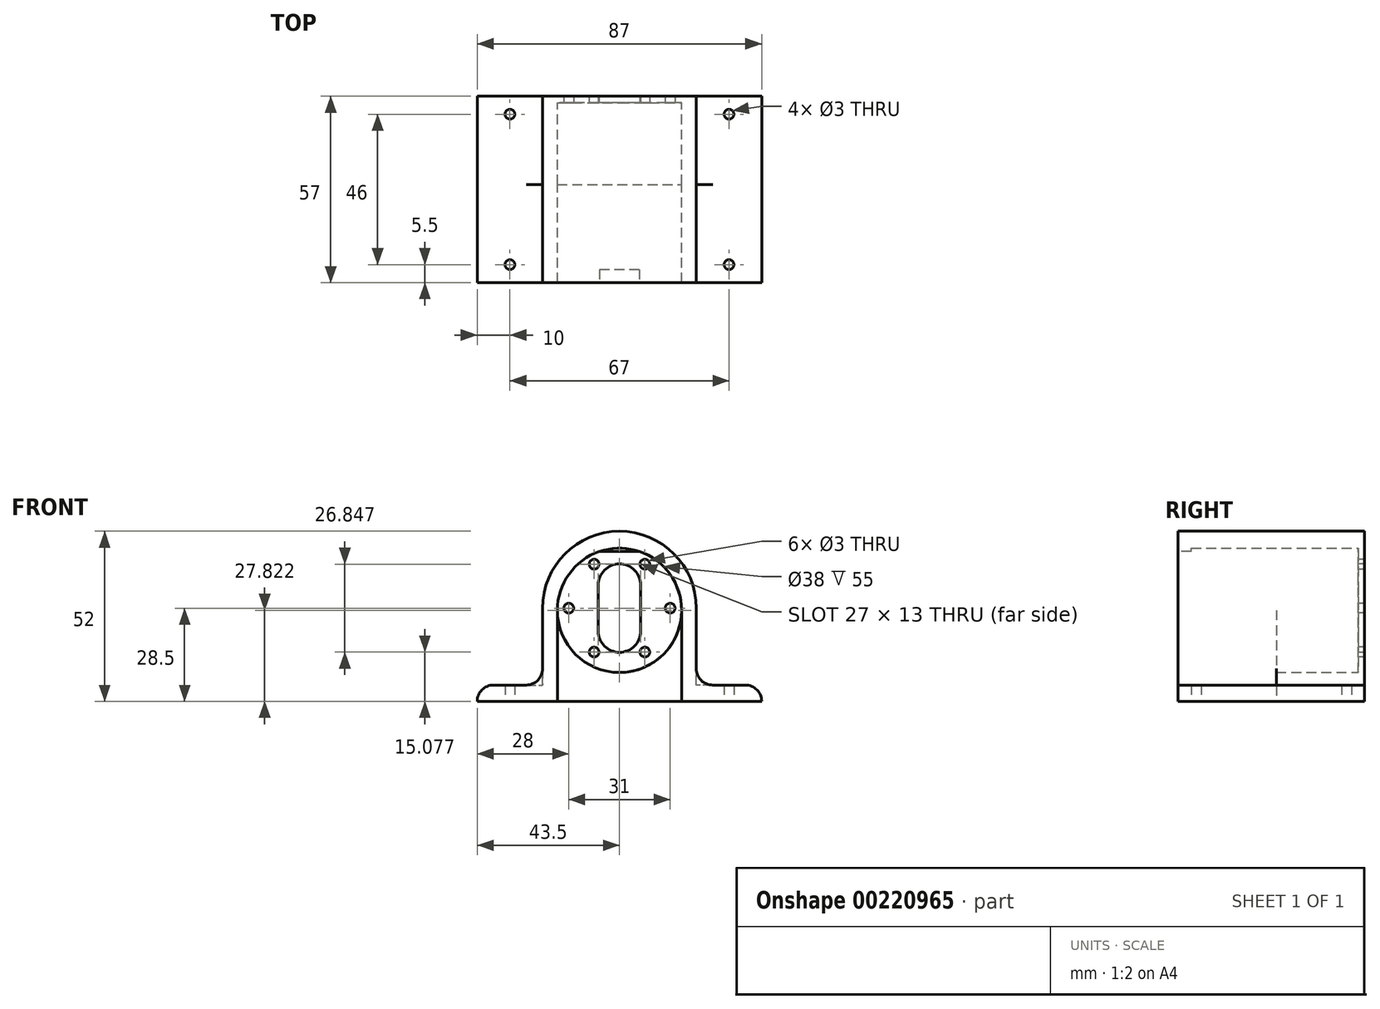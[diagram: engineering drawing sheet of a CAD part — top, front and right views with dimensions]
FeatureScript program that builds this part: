
annotation { "Feature Type Name" : "Feature", "Feature Type Description" : "" }
export const myFeature = defineFeature(function(context is Context, id is Id, definition is map)
    precondition{}
    {
        {
            var Q0;
            Q0=qCreatedBy(makeId("Front.planeOp"),FACE);
            var sketch = newSketch(context, id + "F0", { "sketchPlane" : qUnion([Q0])});
            skLineSegment(sketch, "E0", {"start": v(0, -23.5) * mm, "end": v(-23.5, -23.5) * mm});
            skLineSegment(sketch, "E1", {"start": v(-23.5, -23.5) * mm, "end": v(-23.5, 0) * mm});
            skLineSegment(sketch, "E2", {"start": v(0, -23.5) * mm, "end": v(23.5, -23.5) * mm});
            skLineSegment(sketch, "E3", {"start": v(23.5, -23.5) * mm, "end": v(23.5, 0) * mm});
            skArc(sketch, "E4", {"start": v(-23.5, 0) * mm, "mid": v(0, 23.5) * mm, "end": v(23.5, 0) * mm});
            skSolve(sketch);
        }
        {
            var Q0;
            Q0=qSketchRegion(id+"F0",true);
            extrude(context, id + "F1", {"entities" : qUnion([Q0]), "depth" : 2 * mm});
        }
        {
            var Q0;
            Q0=makeQuery(id+"F1.opExtrude","CAP_FACE",FACE,{"disambiguationData":[OSD([sQuery(id+"F0.wireOp",EDGE,"E0"),sQuery(id+"F0.wireOp",EDGE,"E1"),sQuery(id+"F0.wireOp",EDGE,"E2"),sQuery(id+"F0.wireOp",EDGE,"E3"),sQuery(id+"F0.wireOp",EDGE,"E4")])],"isStart":false});
            var sketch = newSketch(context, id + "F2", { "sketchPlane" : qUnion([Q0])});
            skCircle(sketch, "E5", {"center": v(15.5, 0) * mm, "radius": 1.5 * mm});
            skCircle(sketch, "E6.1.0", {"center": v(7.75, 13.42) * mm, "radius": 1.5 * mm});
            skCircle(sketch, "E6.2.0", {"center": v(-7.75, 13.42) * mm, "radius": 1.5 * mm});
            skCircle(sketch, "E6.3.0", {"center": v(-15.5, 0) * mm, "radius": 1.5 * mm});
            skCircle(sketch, "E6.4.0", {"center": v(-7.75, -13.42) * mm, "radius": 1.5 * mm});
            skCircle(sketch, "E6.5.0", {"center": v(7.75, -13.42) * mm, "radius": 1.5 * mm});
            skPoint(sketch, "E6.center", {"position": v(0, 0) * mm});
            skLineSegment(sketch, "E7", {"start": v(6.5, 7) * mm, "end": v(6.5, -7) * mm});
            skLineSegment(sketch, "E8", {"start": v(-6.5, -7) * mm, "end": v(-6.5, 7) * mm});
            skArc(sketch, "E9", {"start": v(-6.5, 7) * mm, "mid": v(0, 13.5) * mm, "end": v(6.5, 7) * mm});
            skArc(sketch, "E10", {"start": v(-6.5, -7) * mm, "mid": v(0, -13.5) * mm, "end": v(6.5, -7) * mm});
            skSolve(sketch);
        }
        {
            var Q0;
            Q0=qSketchRegion(id+"F2",true);
            extrude(context, id + "F3", {"entities" : qUnion([Q0]), "operationType" : NewBodyOperationType.REMOVE, "oppositeDirection" : true, "depth" : 5 * mm});
        }
        {
            var Q0;
            Q0=qCreatedBy(makeId("Front.planeOp"),FACE);
            var sketch = newSketch(context, id + "F4", { "sketchPlane" : qUnion([Q0])});
            skCircle(sketch, "E11", {"center": v(0, -0.68) * mm, "radius": 19 * mm});
            skLineSegment(sketch, "E12", {"start": v(-23.5, 0) * mm, "end": v(-23.5, -23.5) * mm});
            skLineSegment(sketch, "E13", {"start": v(-23.5, -23.5) * mm, "end": v(23.5, -23.5) * mm});
            skLineSegment(sketch, "E14", {"start": v(23.5, -23.5) * mm, "end": v(23.5, 0) * mm});
            skArc(sketch, "E15", {"start": v(-23.5, 0) * mm, "mid": v(0, 23.5) * mm, "end": v(23.5, 0) * mm});
            skSolve(sketch);
        }
        {
            var Q0;
            Q0=qSketchRegion(id+"F4",true);
            extrude(context, id + "F5", {"entities" : qUnion([Q0]), "operationType" : NewBodyOperationType.ADD, "offsetDistance" : 25 * mm, "depth" : 27 * mm});
        }
        {
            var Q0;
            Q0=makeQuery(id+"F5.boolean.opBoolean","MERGE",FACE,{"derivedFrom":[makeQuery(id+"F1.opExtrude","SWEPT_FACE",FACE,{"disambiguationData":[OSD([sQuery(id+"F0.wireOp",EDGE,"E0"),sQuery(id+"F0.wireOp",EDGE,"E2")])]}),makeQuery(id+"F5.opExtrude","SWEPT_FACE",FACE,{"disambiguationData":[OSD([sQuery(id+"F4.wireOp",EDGE,"E13")])]})]});
            var sketch = newSketch(context, id + "F6", { "sketchPlane" : qUnion([Q0])});
            skLineSegment(sketch, "E16.bottom", {"start": v(-23.5, 27) * mm, "end": v(23.5, 27) * mm});
            skLineSegment(sketch, "E16.top", {"start": v(-23.5, 0) * mm, "end": v(23.5, 0) * mm});
            skLineSegment(sketch, "E16.left", {"start": v(-23.5, 27) * mm, "end": v(-23.5, 0) * mm});
            skLineSegment(sketch, "E16.right", {"start": v(23.5, 27) * mm, "end": v(23.5, 0) * mm});
            skSolve(sketch);
        }
        {
            var Q0;
            Q0=qSketchRegion(id+"F6",true);
            extrude(context, id + "F7", {"entities" : qUnion([Q0]), "operationType" : NewBodyOperationType.ADD, "depth" : 5 * mm});
        }
        {
            var Q0;
            Q0=makeQuery(id+"F7.boolean.opBoolean","MERGE",FACE,{"derivedFrom":[makeQuery(id+"F5.boolean.opBoolean","MERGE",FACE,{"derivedFrom":[makeQuery(id+"F1.opExtrude","SWEPT_FACE",FACE,{"disambiguationData":[OSD([sQuery(id+"F0.wireOp",EDGE,"E1")])]}),makeQuery(id+"F5.opExtrude","SWEPT_FACE",FACE,{"disambiguationData":[OSD([sQuery(id+"F4.wireOp",EDGE,"E12")])]})]}),makeQuery(id+"F7.opExtrude","SWEPT_FACE",FACE,{"disambiguationData":[OSD([sQuery(id+"F6.wireOp",EDGE,"E16.left")])]})]});
            var sketch = newSketch(context, id + "F8", { "sketchPlane" : qUnion([Q0])});
            skLineSegment(sketch, "E17.bottom", {"start": v(0, -28.5) * mm, "end": v(27, -28.5) * mm});
            skLineSegment(sketch, "E17.top", {"start": v(0, -23.5) * mm, "end": v(27, -23.5) * mm});
            skLineSegment(sketch, "E17.left", {"start": v(0, -28.5) * mm, "end": v(0, -23.5) * mm});
            skLineSegment(sketch, "E17.right", {"start": v(27, -28.5) * mm, "end": v(27, -23.5) * mm});
            skSolve(sketch);
        }
        {
            var Q0;
            Q0=qSketchRegion(id+"F8",true);
            extrude(context, id + "F9", {"entities" : qUnion([Q0]), "operationType" : NewBodyOperationType.ADD, "depth" : 20 * mm});
        }
        {
            var Q0;
            Q0=makeQuery(id+"F7.boolean.opBoolean","MERGE",FACE,{"derivedFrom":[makeQuery(id+"F5.boolean.opBoolean","MERGE",FACE,{"derivedFrom":[makeQuery(id+"F1.opExtrude","SWEPT_FACE",FACE,{"disambiguationData":[OSD([sQuery(id+"F0.wireOp",EDGE,"E3")])]}),makeQuery(id+"F5.opExtrude","SWEPT_FACE",FACE,{"disambiguationData":[OSD([sQuery(id+"F4.wireOp",EDGE,"E14")])]})]}),makeQuery(id+"F7.opExtrude","SWEPT_FACE",FACE,{"disambiguationData":[OSD([sQuery(id+"F6.wireOp",EDGE,"E16.right")])]})]});
            var sketch = newSketch(context, id + "F10", { "sketchPlane" : qUnion([Q0])});
            skLineSegment(sketch, "E18.bottom", {"start": v(-27, -28.5) * mm, "end": v(0, -28.5) * mm});
            skLineSegment(sketch, "E18.top", {"start": v(-27, -23.5) * mm, "end": v(0, -23.5) * mm});
            skLineSegment(sketch, "E18.left", {"start": v(-27, -28.5) * mm, "end": v(-27, -23.5) * mm});
            skLineSegment(sketch, "E18.right", {"start": v(0, -28.5) * mm, "end": v(0, -23.5) * mm});
            skSolve(sketch);
        }
        {
            var Q0;
            Q0=qSketchRegion(id+"F10",true);
            extrude(context, id + "F11", {"entities" : qUnion([Q0]), "operationType" : NewBodyOperationType.ADD, "depth" : 20 * mm});
        }
        {
            var Q0;
            Q0=makeQuery(id+"F11.opExtrude","CAP_EDGE",EDGE,{"disambiguationData":[OSD([sQuery(id+"F10.wireOp",EDGE,"E18.top")])],"isStart":true});
            var Q1;
            Q1=makeQuery(id+"F11.opExtrude","CAP_EDGE",EDGE,{"disambiguationData":[OSD([sQuery(id+"F10.wireOp",EDGE,"E18.top")])],"isStart":false});
            var Q2;
            Q2=makeQuery(id+"F9.opExtrude","CAP_EDGE",EDGE,{"disambiguationData":[OSD([sQuery(id+"F8.wireOp",EDGE,"E17.top")])],"isStart":true});
            var Q3;
            Q3=makeQuery(id+"F9.opExtrude","CAP_EDGE",EDGE,{"disambiguationData":[OSD([sQuery(id+"F8.wireOp",EDGE,"E17.top")])],"isStart":false});
            fillet(context, id + "F12", {"entities" : qUnion([Q0, Q1, Q2, Q3]), "radius" : 5 * mm, "tangentPropagation" : true, "allowEdgeOverflow" : false});
        }
        {
            var Q0;
            Q0=makeQuery(id+"F11.boolean.opBoolean","MERGE",FACE,{"derivedFrom":[makeQuery(id+"F9.boolean.opBoolean","MERGE",FACE,{"derivedFrom":[makeQuery(id+"F7.boolean.opBoolean","MERGE",FACE,{"derivedFrom":[makeQuery(id+"F5.opExtrude","CAP_FACE",FACE,{"disambiguationData":[OSD([sQuery(id+"F4.wireOp",EDGE,"E11"),sQuery(id+"F4.wireOp",EDGE,"E12"),sQuery(id+"F4.wireOp",EDGE,"E13"),sQuery(id+"F4.wireOp",EDGE,"E14"),sQuery(id+"F4.wireOp",EDGE,"E15")])],"isStart":false}),makeQuery(id+"F7.opExtrude","SWEPT_FACE",FACE,{"disambiguationData":[OSD([sQuery(id+"F6.wireOp",EDGE,"E16.bottom")])]})]}),makeQuery(id+"F9.opExtrude","SWEPT_FACE",FACE,{"disambiguationData":[OSD([sQuery(id+"F8.wireOp",EDGE,"E17.right")])]})]}),makeQuery(id+"F11.opExtrude","SWEPT_FACE",FACE,{"disambiguationData":[OSD([sQuery(id+"F10.wireOp",EDGE,"E18.left")])]})]});
            var sketch = newSketch(context, id + "F13", { "sketchPlane" : qUnion([Q0])});
            skLineSegment(sketch, "E19", {"start": v(0, -19.68) * mm, "end": v(0, -0.68) * mm});
            skArc(sketch, "E20", {"start": v(23.5, 0) * mm, "mid": v(0, 23.5) * mm, "end": v(-23.5, 0) * mm});
            skLineSegment(sketch, "E21", {"start": v(-23.5, 0) * mm, "end": v(-23.5, -18.5) * mm});
            skLineSegment(sketch, "E22", {"start": v(23.5, 0) * mm, "end": v(23.5, -18.5) * mm});
            skArc(sketch, "E23", {"start": v(-23.5, -18.5) * mm, "mid": v(-24.96, -22.04) * mm, "end": v(-28.5, -23.5) * mm});
            skLineSegment(sketch, "E24", {"start": v(-28.5, -23.5) * mm, "end": v(-38.5, -23.5) * mm});
            skArc(sketch, "E25", {"start": v(-38.5, -23.5) * mm, "mid": v(-42.04, -24.96) * mm, "end": v(-43.5, -28.5) * mm});
            skLineSegment(sketch, "E26", {"start": v(-19, -0.68) * mm, "end": v(-19, -28.5) * mm});
            skLineSegment(sketch, "E27", {"start": v(-19, -28.5) * mm, "end": v(-43.5, -28.5) * mm});
            skLineSegment(sketch, "E28", {"start": v(19, -0.68) * mm, "end": v(19, -28.5) * mm});
            skLineSegment(sketch, "E29", {"start": v(19, -28.5) * mm, "end": v(43.5, -28.5) * mm});
            skArc(sketch, "E30", {"start": v(19, -0.68) * mm, "mid": v(0, 18.32) * mm, "end": v(-19, -0.68) * mm});
            skArc(sketch, "E31", {"start": v(23.5, -18.5) * mm, "mid": v(24.96, -22.04) * mm, "end": v(28.5, -23.5) * mm});
            skLineSegment(sketch, "E32", {"start": v(28.5, -23.5) * mm, "end": v(38.5, -23.5) * mm});
            skArc(sketch, "E33", {"start": v(38.5, -23.5) * mm, "mid": v(42.04, -24.96) * mm, "end": v(43.5, -28.5) * mm});
            skSolve(sketch);
        }
        {
            var Q0;
            Q0 = qSketchRegion(id + "F13", true);
            extrude(context, id + "F14", {"entities" : qUnion([Q0]), "operationType" : NewBodyOperationType.ADD, "depth" : 30 * mm, "offsetDistance" : 25 * mm});
        }
        {
            var Q0;
            Q0=makeQuery(id+"F14.opExtrude","CAP_FACE",FACE,{"disambiguationData":[OSD([sQuery(id+"F13.wireOp",EDGE,"E20"),sQuery(id+"F13.wireOp",EDGE,"E21"),sQuery(id+"F13.wireOp",EDGE,"E22"),sQuery(id+"F13.wireOp",EDGE,"E23"),sQuery(id+"F13.wireOp",EDGE,"f846ae2c-578c-465c-87cc-d48e436d984c"),sQuery(id+"F13.wireOp",EDGE,"VP23P4Di-zLj5-c1Cz-1IMT-ZziUseBplQmi"),sQuery(id+"F13.wireOp",EDGE,"E24"),sQuery(id+"F13.wireOp",EDGE,"E25"),sQuery(id+"F13.wireOp",EDGE,"366fcdaa-7b72-4651-9bb5-7b83db4a8332"),sQuery(id+"F13.wireOp",EDGE,"E26"),sQuery(id+"F13.wireOp",EDGE,"E27"),sQuery(id+"F13.wireOp",EDGE,"E28"),sQuery(id+"F13.wireOp",EDGE,"E29"),sQuery(id+"F13.wireOp",EDGE,"E30")])],"isStart":false});
            var sketch = newSketch(context, id + "F15", { "sketchPlane" : qUnion([Q0])});
            skLineSegment(sketch, "E34", {"start": v(0, 18.32) * mm, "end": v(0, 17.32) * mm});
            skLineSegment(sketch, "E35", {"start": v(0, 17.32) * mm, "end": v(-6.08, 17.32) * mm});
            skLineSegment(sketch, "E36", {"start": v(0, 17.32) * mm, "end": v(6.08, 17.32) * mm});
            skArc(sketch, "E37", {"start": v(6.08, 17.32) * mm, "mid": v(0, 18.32) * mm, "end": v(-6.08, 17.32) * mm});
            skSolve(sketch);
        }
        {
            var Q0;
            Q0 = qSketchRegion(id + "F15", true);
            extrude(context, id + "F16", {"entities" : qUnion([Q0]), "operationType" : NewBodyOperationType.ADD, "oppositeDirection" : true, "depth" : 4 * mm, "offsetDistance" : 25 * mm});
        }
        {
            var Q0;
            Q0=makeQuery(id+"F14.boolean.opBoolean","MERGE",FACE,{"derivedFrom":[makeQuery(id+"F11.boolean.opBoolean","MERGE",FACE,{"derivedFrom":[makeQuery(id+"F9.boolean.opBoolean","MERGE",FACE,{"derivedFrom":[makeQuery(id+"F7.opExtrude","CAP_FACE",FACE,{"disambiguationData":[OSD([sQuery(id+"F6.wireOp",EDGE,"E16.bottom"),sQuery(id+"F6.wireOp",EDGE,"E16.top"),sQuery(id+"F6.wireOp",EDGE,"E16.left"),sQuery(id+"F6.wireOp",EDGE,"E16.right")])],"isStart":false}),makeQuery(id+"F9.opExtrude","SWEPT_FACE",FACE,{"disambiguationData":[OSD([sQuery(id+"F8.wireOp",EDGE,"E17.bottom")])]})]}),makeQuery(id+"F11.opExtrude","SWEPT_FACE",FACE,{"disambiguationData":[OSD([sQuery(id+"F10.wireOp",EDGE,"E18.bottom")])]})]}),makeQuery(id+"F14.opExtrude","SWEPT_FACE",FACE,{"disambiguationData":[OSD([sQuery(id+"F13.wireOp",EDGE,"E27")])]}),makeQuery(id+"F14.opExtrude","SWEPT_FACE",FACE,{"disambiguationData":[OSD([sQuery(id+"F13.wireOp",EDGE,"E29")])]})]});
            var sketch = newSketch(context, id + "F17", { "sketchPlane" : qUnion([Q0])});
            skLineSegment(sketch, "E38", {"start": v(-43.5, 0) * mm, "end": v(-33.5, 0) * mm});
            skLineSegment(sketch, "E39", {"start": v(-33.5, 0) * mm, "end": v(-33.5, 5.5) * mm});
            skLineSegment(sketch, "E40", {"start": v(-33.5, 51.5) * mm, "end": v(33.5, 51.5) * mm});
            skCircle(sketch, "E41", {"center": v(-33.5, 51.5) * mm, "radius": 1.5 * mm});
            skCircle(sketch, "E42", {"center": v(-33.5, 5.5) * mm, "radius": 1.5 * mm});
            skCircle(sketch, "E43", {"center": v(33.5, 5.5) * mm, "radius": 1.5 * mm});
            skCircle(sketch, "E44", {"center": v(33.5, 51.5) * mm, "radius": 1.5 * mm});
            skLineSegment(sketch, "E45", {"start": v(-33.5, 51.5) * mm, "end": v(-33.5, 57) * mm});
            skLineSegment(sketch, "E46", {"start": v(33.5, 5.5) * mm, "end": v(-33.5, 5.5) * mm});
            skLineSegment(sketch, "E47", {"start": v(-43.5, 28.5) * mm, "end": v(43.5, 28.5) * mm});
            skLineSegment(sketch, "E48", {"start": v(43.5, 57) * mm, "end": v(43.5, 0) * mm});
            skLineSegment(sketch, "E49", {"start": v(-33.5, 5.5) * mm, "end": v(-43.5, 5.5) * mm});
            skLineSegment(sketch, "E50", {"start": v(-33.5, 5.5) * mm, "end": v(-33.5, 51.5) * mm});
            skSolve(sketch);
        }
        {
            var Q0;
            Q0 = qSketchRegion(id + "F17", true);
            extrude(context, id + "F18", {"entities" : qUnion([Q0]), "operationType" : NewBodyOperationType.REMOVE, "oppositeDirection" : true, "depth" : 25 * mm, "offsetDistance" : 25 * mm});
        }
    });
